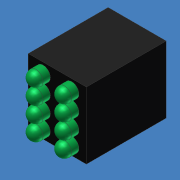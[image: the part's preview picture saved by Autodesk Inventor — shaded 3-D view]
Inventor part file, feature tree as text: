
AUTODESK INVENTOR PART (.ipt)
format: ipt  version: unknown  size: 224,256 bytes
history: native  units: mm (DEFAULTED — no unit token found)
features: extrude x2, sketch x2, fillet x1, pattern_linear x1
ambient origin geometry x8: Origin, YZ Plane, XZ Plane, XY Plane, X Axis, Y Axis, Z Axis, Center Point
feature tree (6):
  extrude  "Extrusion1"  Depth=11.684mm
  extrude  "Extrusion2"  Depth=2.5908mm
  fillet  "Fillet1"  Radius=1.7145mm
  pattern_linear  "Rectangular Pattern1"  Spacing1=2.54mm  [1 undecoded]
  sketch  "Sketch1"  dims[d0=10.16mm d1=11.684mm]
  sketch  "Sketch2"  dims[d2=13.97mm d3=0.0mm d4=2.5908mm d5=1.7145mm d6=2.54mm d7=2.54mm d8=0.0mm d9=1.27mm d10=40.0mm d12=2.75mm d13=20.0mm d15=5.0mm]
note: 1 required parameter value undecoded (feature->parameter linkage not recoverable at this tier; creation-order binding heuristic only, values carry confidence <= 0.55)
